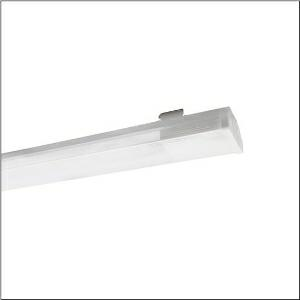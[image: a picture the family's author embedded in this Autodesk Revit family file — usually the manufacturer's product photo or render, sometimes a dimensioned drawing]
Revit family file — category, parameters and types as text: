
# Revit family: modario_31_gen_2_53bm8137u4l3d2_4ea8
name_source: partatom
category: Lighting Fixtures
units: mm (PartAtom-declared; Revit-internal decimal feet)

## family parameters
Cut with Voids When Loaded = No
Host = Face
Light Source = No
Part Type = Normal
Room Calculation Point = No
Round Connector Dimension = Use Diameter
Shared = No

## types (1)
- Modario 31 Gen.2 (1 x LED, 23060 lm, 126 W, 4000K)
    Apparent Load = 126 VA
    CIE Flux Codes = 62 83 95 93 100
    Color Rendering = 80
    Color Temperature = 4000K
    Default Elevation = 1800 mm
    Description = Modario 31 Gen.2, luminaire insert, of sheet steel, coil coated, white, length: 2.392mm, width: 81mm, height: 82mm, 8x system unit, system units: 299mm, LED rated luminous flux: 23.060lm, light colour: 840, SDCM (Standard Deviation of Colour Matching)MacAdam ≤ 3 SDCM (initial), control gear: ON/OFF, with plug, 3-pole, with phase selection, mains connection: 220..240V, AC, 50/60Hz, rated input power: 126W, through-wiring accessed according to module size, primary optical cover: cover, of PMMA, light emission: direct distribution, primary light characteristic: symmetric, protection rating (complete): IP20, protection rating (LED compartment): IP50, insulation class (complete): insulation class I (protective earthing), certification: CE, ENEC, VDE, UKCA, impact resistance: IK03, permissible ambient temperature for indoor applications: -40..+35°C, corresponds to IFS (International Featured Standards) requirements for safety and quality in the food industry, reducing of maximum allowable ambient temperature of 5°C with ceiling mounting, IP40 when using the optional accessory 5TP9018, packaging unit: 1 piece
    Height = 92 mm
    Lamp = 1 x LED
    Lamp Light Flux = 23060 lm
    Lamp Power = 126 W
    Lamp count = 1
    Length = 2392 mm
    Luminous efficacy = 183 lm/W
    Manufacturer = Siteco
    ModVariant = No
    Model = 53BM8137U4L3D2
    Mounting Place = Ceiling
    Mounting Type = Pendant
    Number of Poles = 1
    OnlyDefault = Yes
    Power Factor = 1
    Product Name = Modario 31 Gen.2
    Product group = luminaire insert | ceiling pendant
    ProductGroupID = 901
    Protection Class = Protection class I
    Protection Degree = IP 20
    RLX_Detail_Level = 1
    RLX_Emergency_Light_Flux = 0 lm
    RLX_Emergency_Type = 0
    RLX_Emergency_Type_DB = No
    RlxData = <blob elided: 34809 chars, md5=e2b99543>
    Socket = socket
    Standby Power = 0 W
    System Light Flux = 23061 lm
    System Power = 126 W
    Type Comments = Product without accessories
    Type Image = l_1341883.jpg
    URL = http://relux.com
    VarID = ---
    Voltage = 0 V
    Weight = 0.00 kg
    Width = 81 mm

## geometry (parser evidence)
native form markers: Blend x4, Sweep x12
no freeform markers — native parametric forms only
